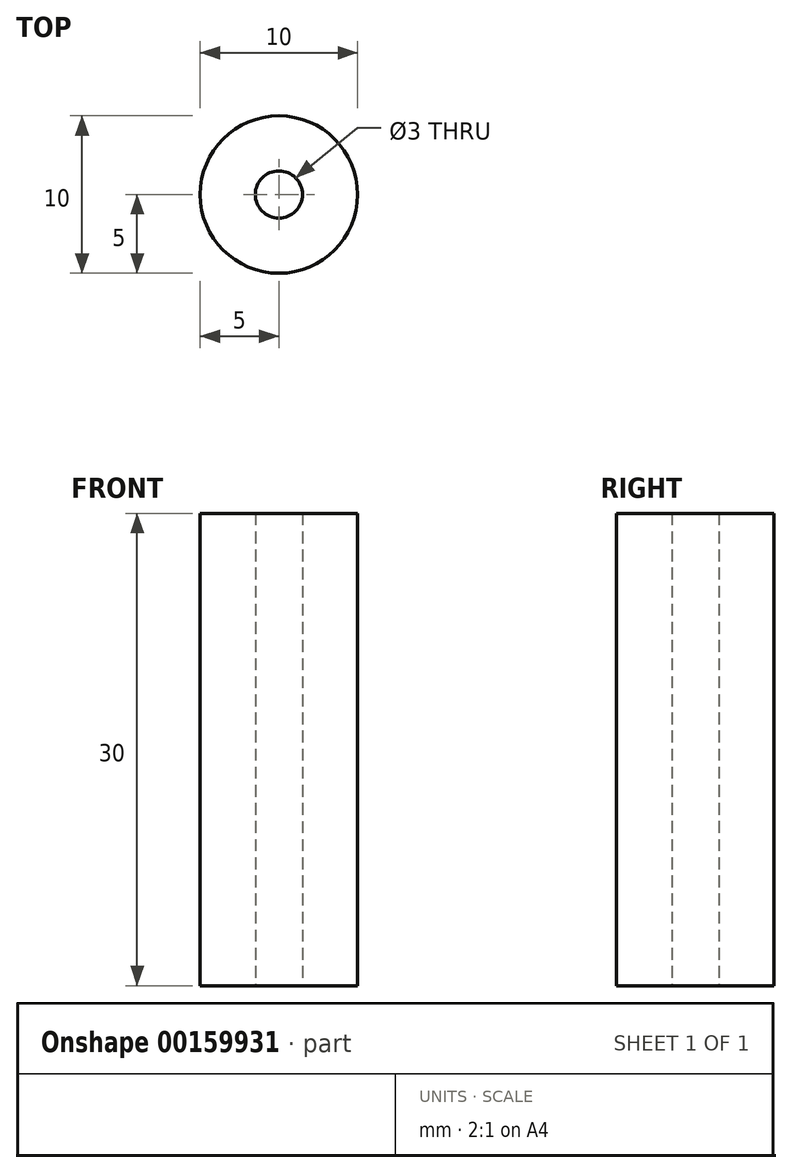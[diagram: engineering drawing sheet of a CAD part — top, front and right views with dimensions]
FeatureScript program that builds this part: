
annotation { "Feature Type Name" : "Feature", "Feature Type Description" : "" }
export const myFeature = defineFeature(function(context is Context, id is Id, definition is map)
    precondition{}
    {
        {
            var Q0;
            Q0=qCreatedBy(makeId("Top.planeOp"),FACE);
            var sketch = newSketch(context, id + "F0", { "sketchPlane" : qUnion([Q0])});
            skCircle(sketch, "E0", {"center": v(0, 0) * mm, "radius": 1.5 * mm});
            skCircle(sketch, "E1", {"center": v(0, 0) * mm, "radius": 5 * mm});
            skSolve(sketch);
        }
        {
            var Q0;
            Q0=makeQuery(id+"F0.imprint","IMPRINT",FACE,{"disambiguationData":[TD([[makeQuery(id+"F0.imprint","IMPRINT",EDGE,{"derivedFrom":sQuery(id+"F0.wireOp",EDGE,"E0")}),-1.0]])]});
            extrude(context, id + "F1", {"entities" : qUnion([Q0]), "depth" : 30 * mm});
        }
    });
